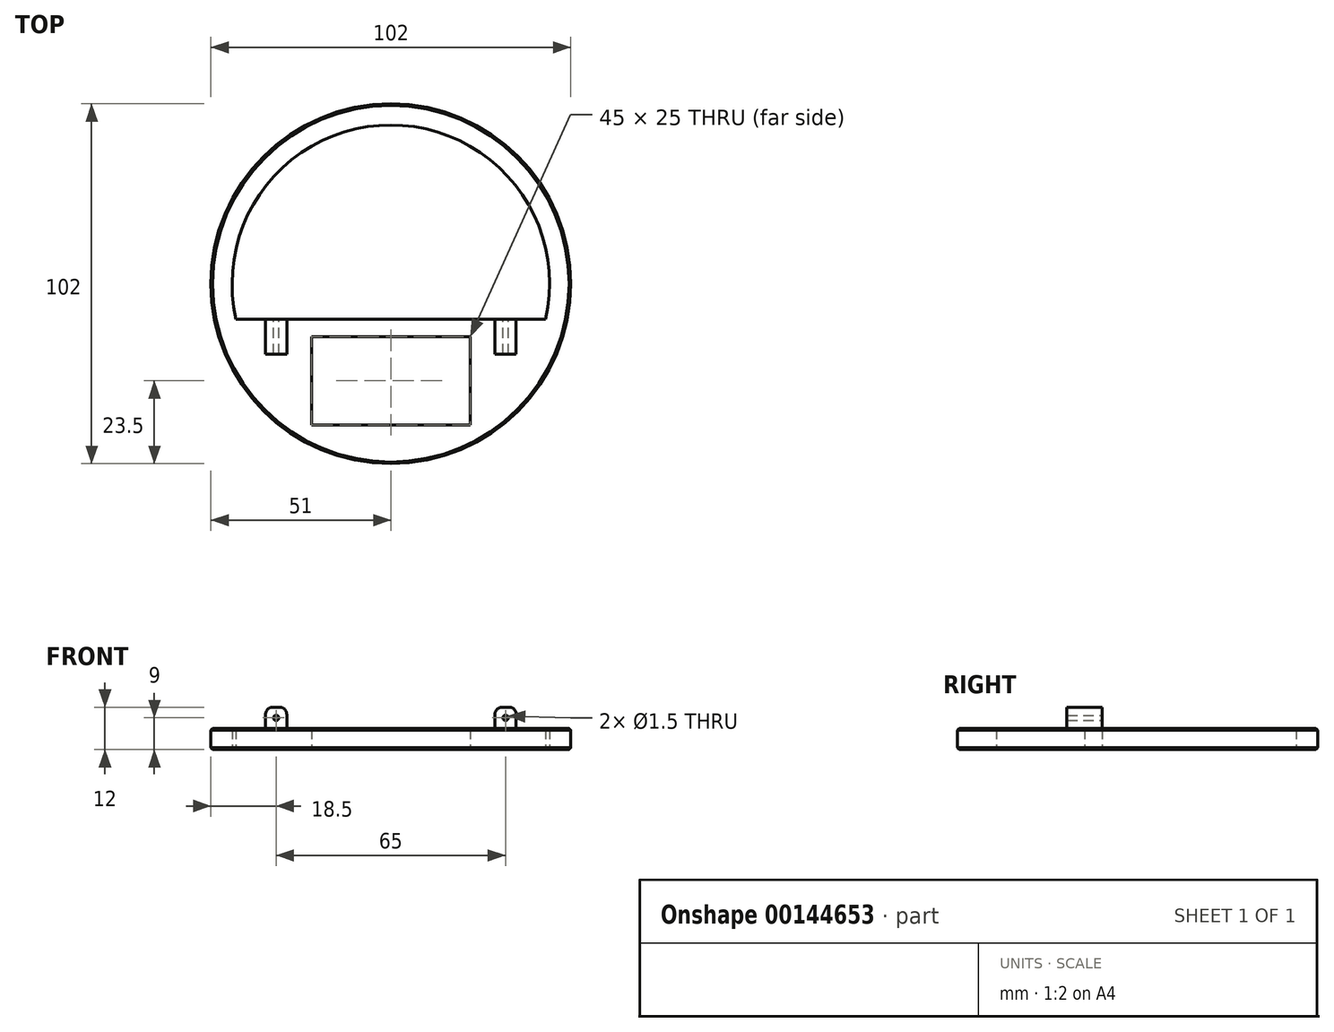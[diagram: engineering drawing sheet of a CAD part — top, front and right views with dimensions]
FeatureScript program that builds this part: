
annotation { "Feature Type Name" : "Feature", "Feature Type Description" : "" }
export const myFeature = defineFeature(function(context is Context, id is Id, definition is map)
    precondition{}
    {
        {
            var Q0;
            Q0=qCreatedBy(makeId("Top.planeOp"),FACE);
            var sketch = newSketch(context, id + "F0", { "sketchPlane" : qUnion([Q0])});
            skCircle(sketch, "E0", {"center": v(0, 0) * mm, "radius": 51 * mm});
            skLineSegment(sketch, "E1", {"start": v(-43.87, -10) * mm, "end": v(43.87, -10) * mm});
            skLineSegment(sketch, "E2.bottom", {"start": v(-22.5, -15) * mm, "end": v(22.5, -15) * mm});
            skLineSegment(sketch, "E2.top", {"start": v(-22.5, -40) * mm, "end": v(22.5, -40) * mm});
            skLineSegment(sketch, "E2.left", {"start": v(-22.5, -15) * mm, "end": v(-22.5, -40) * mm});
            skLineSegment(sketch, "E2.right", {"start": v(22.5, -15) * mm, "end": v(22.5, -40) * mm});
            skPoint(sketch, "E3", {"position": v(0, -15) * mm});
            skArc(sketch, "E4", {"start": v(-43.87, -10) * mm, "mid": v(0, 45) * mm, "end": v(43.87, -10) * mm});
            skSolve(sketch);
        }
        {
            var Q0;
            Q0=makeQuery(id+"F0.imprint","IMPRINT",FACE,{"disambiguationData":[TD([[makeQuery(id+"F0.imprint","IMPRINT",EDGE,{"derivedFrom":sQuery(id+"F0.wireOp",EDGE,"E0")}),1.0]])]});
            extrude(context, id + "F1", {"entities" : qUnion([Q0]), "depth" : 6 * mm});
        }
        {
            var Q0;
            Q0=makeQuery(id+"F1.opExtrude","CAP_FACE",FACE,{"disambiguationData":[OSD([sQuery(id+"F0.wireOp",EDGE,"E0"),sQuery(id+"F0.wireOp",EDGE,"E1"),sQuery(id+"F0.wireOp",EDGE,"E2.bottom"),sQuery(id+"F0.wireOp",EDGE,"E2.top"),sQuery(id+"F0.wireOp",EDGE,"E2.left"),sQuery(id+"F0.wireOp",EDGE,"E2.right"),sQuery(id+"F0.wireOp",EDGE,"E4")])],"isStart":false});
            var sketch = newSketch(context, id + "F2", { "sketchPlane" : qUnion([Q0])});
            skPoint(sketch, "E5", {"position": v(-32.5, -10) * mm});
            skLineSegment(sketch, "E6.bottom", {"start": v(-29.5, -20) * mm, "end": v(-35.5, -20) * mm});
            skLineSegment(sketch, "E6.top", {"start": v(-29.5, 0) * mm, "end": v(-35.5, 0) * mm});
            skLineSegment(sketch, "E6.left", {"start": v(-29.5, -20) * mm, "end": v(-29.5, 0) * mm});
            skLineSegment(sketch, "E6.right", {"start": v(-35.5, -20) * mm, "end": v(-35.5, 0) * mm});
            skSolve(sketch);
        }
        {
            var Q0;
            {var subQ0=sQuery(id+"F2.wireOp",EDGE,"E6.bottom");Q0=makeQuery(id+"F2.imprint","IMPRINT",FACE,{"disambiguationData":[TD([[makeQuery(id+"F2.imprint","IMPRINT",EDGE,{"derivedFrom":subQ0}),-1.0]])]});}
            extrude(context, id + "F3", {"entities" : qUnion([Q0]), "depth" : 6 * mm});
        }
        {
            var Q0;
            {var subQ0=sQuery(id+"F0.wireOp",EDGE,"E1");Q0=makeQuery(id+"F3.boolean.opBoolean","MERGE",FACE,{"derivedFrom":[makeQuery(id+"F1.opExtrude","SWEPT_FACE",FACE,{"disambiguationData":[OSD([subQ0])]}),makeQuery(id+"F3.opExtrude","SWEPT_FACE",FACE,{"disambiguationData":[OSD([subQ0])]})]});}
            var sketch = newSketch(context, id + "F4", { "sketchPlane" : qUnion([Q0])});
            skLineSegment(sketch, "E7", {"start": v(35.5, 6) * mm, "end": v(29.5, 12) * mm});
            skPoint(sketch, "E8", {"position": v(32.5, 9) * mm});
            skSolve(sketch);
        }
        {
            var Q0;
            Q0=makeQuery(id+"F3.opExtrude","CAP_EDGE",EDGE,{"disambiguationData":[OSD([sQuery(id+"F2.wireOp",EDGE,"E6.left")])],"isStart":false});
            var Q1;
            Q1=makeQuery(id+"F3.opExtrude","CAP_EDGE",EDGE,{"disambiguationData":[OSD([sQuery(id+"F2.wireOp",EDGE,"E6.right")])],"isStart":false});
            fillet(context, id + "F5", {"entities" : qUnion([Q0, Q1]), "radius" : 2 * mm, "tangentPropagation" : true, "allowEdgeOverflow" : false});
        }
        {
            var Q0;
            Q0=sQuery(id+"F4.wireOp",VERTEX,"E8");
            var Q1;
            Q1=makeQuery(id+"F3.opExtrude","SWEPT_BODY",BODY,{"disambiguationData":[OSD([sQuery(id+"F0.wireOp",EDGE,"E1"),sQuery(id+"F2.wireOp",EDGE,"E6.bottom"),sQuery(id+"F2.wireOp",EDGE,"E6.left"),sQuery(id+"F2.wireOp",EDGE,"E6.right")])]});
            hole(context, id + "F6", {"style" : HoleStyle.SIMPLE, "endStyle" : HoleEndStyle.THROUGH, "holeDiameter" : 1.5 * mm, "startFromSketch" : true, "locations" : qUnion([Q0]), "scope" : qUnion([Q1]), "isTappedThrough" : true});
        }
        {
            var Q0;
            Q0=makeQuery(id+"F3.opExtrude","SWEPT_BODY",BODY,{"disambiguationData":[OSD([sQuery(id+"F0.wireOp",EDGE,"E1"),sQuery(id+"F2.wireOp",EDGE,"E6.bottom"),sQuery(id+"F2.wireOp",EDGE,"E6.left"),sQuery(id+"F2.wireOp",EDGE,"E6.right")])]});
            var Q1;
            Q1=qCreatedBy(makeId("Right.planeOp"),FACE);
            mirror(context, id + "F7", {"operationType" : NewBodyOperationType.ADD, "entities" : qUnion([Q0]), "mirrorPlane" : qUnion([Q1])});
        }
        {
            var Q0;
            Q0=makeQuery(id+"F1.opExtrude","CAP_EDGE",EDGE,{"disambiguationData":[OSD([sQuery(id+"F0.wireOp",EDGE,"E0")])],"isStart":false});
            var Q1;
            Q1=makeQuery(id+"F1.opExtrude","CAP_EDGE",EDGE,{"disambiguationData":[OSD([sQuery(id+"F0.wireOp",EDGE,"E0")])],"isStart":true});
            chamfer(context, id + "F8", {"entities" : qUnion([Q0, Q1]), "width" : 0.5 * mm, "tangentPropagation" : true});
        }
    });
